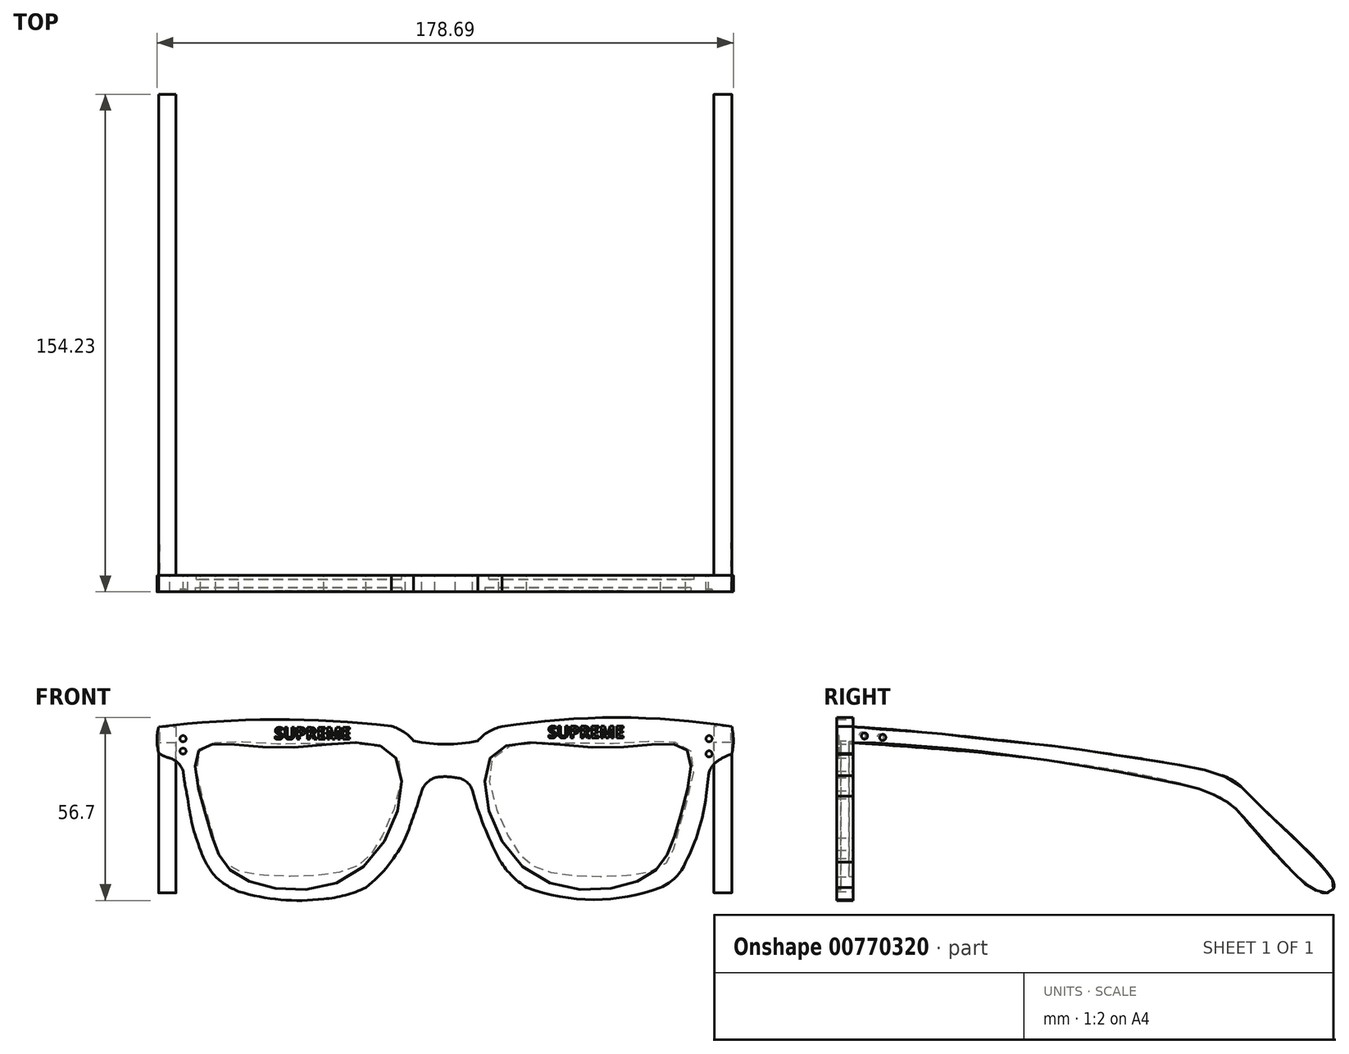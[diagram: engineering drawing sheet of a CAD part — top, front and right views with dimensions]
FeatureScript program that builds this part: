
annotation { "Feature Type Name" : "Feature", "Feature Type Description" : "" }
export const myFeature = defineFeature(function(context is Context, id is Id, definition is map)
    precondition{}
    {
        {
            var Q0;
            Q0=qCreatedBy(makeId("Front.planeOp"),FACE);
            var sketch = newSketch(context, id + "F0", { "sketchPlane" : qUnion([Q0])});
            skArc(sketch, "E0", {"start": v(-13.5, 37.38) * mm, "mid": v(-49.59, 39.43) * mm, "end": v(-85.66, 37.14) * mm});
            skArc(sketch, "E1", {"start": v(-6.56, 32.82) * mm, "mid": v(-9.67, 35.64) * mm, "end": v(-13.5, 37.38) * mm});
            skArc(sketch, "E2", {"start": v(-6.56, 32.82) * mm, "mid": v(3.35, 31.82) * mm, "end": v(13.26, 32.82) * mm});
            skArc(sketch, "E3", {"start": v(20.82, 37.23) * mm, "mid": v(16.66, 35.67) * mm, "end": v(13.26, 32.82) * mm});
            skArc(sketch, "E4", {"start": v(92.01, 37.23) * mm, "mid": v(56.41, 40.06) * mm, "end": v(20.82, 37.23) * mm});
            skArc(sketch, "E5", {"start": v(92.06, 28.92) * mm, "mid": v(92.54, 33.08) * mm, "end": v(92.01, 37.23) * mm});
            skArc(sketch, "E6", {"start": v(77.77, -4.76) * mm, "mid": v(81.8, 5.23) * mm, "end": v(84.08, 15.74) * mm});
            skArc(sketch, "E7", {"start": v(70.01, -12.62) * mm, "mid": v(74.63, -9.42) * mm, "end": v(77.77, -4.76) * mm});
            skArc(sketch, "E8", {"start": v(28.46, -12.62) * mm, "mid": v(49.23, -16.4) * mm, "end": v(70.01, -12.62) * mm});
            skArc(sketch, "E9", {"start": v(19.81, -3.65) * mm, "mid": v(23.57, -8.68) * mm, "end": v(28.46, -12.62) * mm});
            skArc(sketch, "E10", {"start": v(11.61, 17.3) * mm, "mid": v(15.15, 6.6) * mm, "end": v(19.81, -3.65) * mm});
            skArc(sketch, "E11", {"start": v(11.61, 17.3) * mm, "mid": v(9.68, 20.28) * mm, "end": v(6.3, 21.4) * mm});
            skArc(sketch, "E12", {"start": v(6.3, 21.4) * mm, "mid": v(3.15, 21.73) * mm, "end": v(0, 21.4) * mm});
            skArc(sketch, "E13", {"start": v(0, 21.4) * mm, "mid": v(-2.52, 19.8) * mm, "end": v(-4.12, 17.3) * mm});
            skArc(sketch, "E14", {"start": v(-9.1, 2.78) * mm, "mid": v(-6.43, 9.97) * mm, "end": v(-4.12, 17.3) * mm});
            skArc(sketch, "E15", {"start": v(-21.4, -12.62) * mm, "mid": v(-14.35, -5.65) * mm, "end": v(-9.1, 2.78) * mm});
            skArc(sketch, "E16", {"start": v(-34.48, -16.17) * mm, "mid": v(-27.78, -15.01) * mm, "end": v(-21.4, -12.62) * mm});
            skArc(sketch, "E17", {"start": v(-60.86, -13.84) * mm, "mid": v(-47.8, -16.4) * mm, "end": v(-34.48, -16.17) * mm});
            skArc(sketch, "E18", {"start": v(-67.95, -9.3) * mm, "mid": v(-64.61, -11.9) * mm, "end": v(-60.86, -13.84) * mm});
            skArc(sketch, "E19", {"start": v(-72.6, -1.1) * mm, "mid": v(-70.72, -5.45) * mm, "end": v(-67.95, -9.3) * mm});
            skArc(sketch, "E20", {"start": v(-76.6, 14.97) * mm, "mid": v(-75.16, 6.8) * mm, "end": v(-72.6, -1.1) * mm});
            skArc(sketch, "E21", {"start": v(-78.03, 23.4) * mm, "mid": v(-77.42, 19.16) * mm, "end": v(-76.6, 14.97) * mm});
            skArc(sketch, "E22", {"start": v(-78.03, 23.4) * mm, "mid": v(-79.58, 25.94) * mm, "end": v(-82.13, 27.5) * mm});
            skArc(sketch, "E23", {"start": v(-85.57, 29.04) * mm, "mid": v(-83.93, 28.09) * mm, "end": v(-82.13, 27.5) * mm});
            skArc(sketch, "E24", {"start": v(-85.66, 37.14) * mm, "mid": v(-86.15, 33.09) * mm, "end": v(-85.57, 29.04) * mm});
            skArc(sketch, "E25", {"start": v(91.85, 28.69) * mm, "mid": v(89.6, 27.74) * mm, "end": v(87.5, 26.49) * mm});
            skArc(sketch, "E26", {"start": v(91.81, 28.67) * mm, "mid": v(91.98, 28.77) * mm, "end": v(92.06, 28.94) * mm});
            skArc(sketch, "E27", {"start": v(87.5, 26.49) * mm, "mid": v(85.68, 24.53) * mm, "end": v(84.79, 22.01) * mm});
            skLineSegment(sketch, "E28", {"start": v(84.79, 22.01) * mm, "end": v(84.08, 15.74) * mm});
            skSolve(sketch);
        }
        {
            var Q0;
            Q0 = qSketchRegion(id + "F0", true);
            extrude(context, id + "F1", {"entities" : qUnion([Q0]), "depth" : 5.08 * mm, "offsetDistance" : 25.4 * mm});
        }
        {
            var Q0;
            Q0=makeQuery(id+"F1.opExtrude","CAP_FACE",FACE,{"disambiguationData":[OSD([sQuery(id+"F0.wireOp",EDGE,"E0"),sQuery(id+"F0.wireOp",EDGE,"E1"),sQuery(id+"F0.wireOp",EDGE,"E2"),sQuery(id+"F0.wireOp",EDGE,"E3"),sQuery(id+"F0.wireOp",EDGE,"E4"),sQuery(id+"F0.wireOp",EDGE,"E5"),sQuery(id+"F0.wireOp",EDGE,"E6"),sQuery(id+"F0.wireOp",EDGE,"E7"),sQuery(id+"F0.wireOp",EDGE,"E8"),sQuery(id+"F0.wireOp",EDGE,"E9"),sQuery(id+"F0.wireOp",EDGE,"E10"),sQuery(id+"F0.wireOp",EDGE,"E11"),sQuery(id+"F0.wireOp",EDGE,"E12"),sQuery(id+"F0.wireOp",EDGE,"E13"),sQuery(id+"F0.wireOp",EDGE,"E14"),sQuery(id+"F0.wireOp",EDGE,"E15"),sQuery(id+"F0.wireOp",EDGE,"E16"),sQuery(id+"F0.wireOp",EDGE,"E17"),sQuery(id+"F0.wireOp",EDGE,"E18"),sQuery(id+"F0.wireOp",EDGE,"E19"),sQuery(id+"F0.wireOp",EDGE,"E20"),sQuery(id+"F0.wireOp",EDGE,"E21"),sQuery(id+"F0.wireOp",EDGE,"E22"),sQuery(id+"F0.wireOp",EDGE,"E23"),sQuery(id+"F0.wireOp",EDGE,"E24"),sQuery(id+"F0.wireOp",EDGE,"E25"),sQuery(id+"F0.wireOp",EDGE,"E26"),sQuery(id+"F0.wireOp",EDGE,"E27"),sQuery(id+"F0.wireOp",EDGE,"E28")])],"isStart":false});
            var sketch = newSketch(context, id + "F2", { "sketchPlane" : qUnion([Q0])});
            skFitSpline(sketch, "E29", {"points": [v(-73.12, 29.88) * mm, v(-47.85, 30.68) * mm, v(-12.75, 28.55) * mm, v(-23.12, -7.08) * mm, v(-61.02, -8.94) * mm, v(-70.32, 7.4) * mm, v(-73.12, 29.88) * mm]});
            skFitSpline(sketch, "E30.MirrorC", {"points": [v(78.24, 29.88) * mm, v(52.98, 30.68) * mm, v(17.88, 28.55) * mm, v(28.25, -7.08) * mm, v(66.14, -8.94) * mm, v(75.45, 7.4) * mm, v(78.24, 29.88) * mm]});
            skSolve(sketch);
        }
        {
            var Q0;
            Q0 = qSketchRegion(id + "F2", true);
            extrude(context, id + "F3", {"entities" : qUnion([Q0]), "operationType" : NewBodyOperationType.REMOVE, "oppositeDirection" : true, "depth" : 1.27 * mm, "offsetDistance" : 25.4 * mm});
        }
        {
            var Q0;
            Q0=makeQuery(id+"F1.opExtrude","CAP_FACE",FACE,{"disambiguationData":[OSD([sQuery(id+"F0.wireOp",EDGE,"E0"),sQuery(id+"F0.wireOp",EDGE,"E1"),sQuery(id+"F0.wireOp",EDGE,"E2"),sQuery(id+"F0.wireOp",EDGE,"E3"),sQuery(id+"F0.wireOp",EDGE,"E4"),sQuery(id+"F0.wireOp",EDGE,"E5"),sQuery(id+"F0.wireOp",EDGE,"E6"),sQuery(id+"F0.wireOp",EDGE,"E7"),sQuery(id+"F0.wireOp",EDGE,"E8"),sQuery(id+"F0.wireOp",EDGE,"E9"),sQuery(id+"F0.wireOp",EDGE,"E10"),sQuery(id+"F0.wireOp",EDGE,"E11"),sQuery(id+"F0.wireOp",EDGE,"E12"),sQuery(id+"F0.wireOp",EDGE,"E13"),sQuery(id+"F0.wireOp",EDGE,"E14"),sQuery(id+"F0.wireOp",EDGE,"E15"),sQuery(id+"F0.wireOp",EDGE,"E16"),sQuery(id+"F0.wireOp",EDGE,"E17"),sQuery(id+"F0.wireOp",EDGE,"E18"),sQuery(id+"F0.wireOp",EDGE,"E19"),sQuery(id+"F0.wireOp",EDGE,"E20"),sQuery(id+"F0.wireOp",EDGE,"E21"),sQuery(id+"F0.wireOp",EDGE,"E22"),sQuery(id+"F0.wireOp",EDGE,"E23"),sQuery(id+"F0.wireOp",EDGE,"E24"),sQuery(id+"F0.wireOp",EDGE,"E25"),sQuery(id+"F0.wireOp",EDGE,"E26"),sQuery(id+"F0.wireOp",EDGE,"E27"),sQuery(id+"F0.wireOp",EDGE,"E28")])],"isStart":true});
            var sketch = newSketch(context, id + "F4", { "sketchPlane" : qUnion([Q0])});
            skFitSpline(sketch, "E31", {"points": [v(-79.44, 29.57) * mm, v(-53.26, 31.93) * mm, v(-18.19, 27.95) * mm, v(-22.34, 4.15) * mm, v(-31.45, -6.46) * mm, v(-51.31, -9.2) * mm, v(-70.95, -5.77) * mm, v(-75.57, 5.26) * mm, v(-79.44, 29.57) * mm]});
            skFitSpline(sketch, "E32.MirrorC", {"points": [v(73.03, 29.57) * mm, v(46.84, 31.93) * mm, v(11.77, 27.95) * mm, v(15.92, 4.15) * mm, v(25.03, -6.46) * mm, v(44.9, -9.2) * mm, v(64.53, -5.77) * mm, v(69.15, 5.26) * mm, v(73.03, 29.57) * mm]});
            skSolve(sketch);
        }
        {
            var Q0;
            Q0=makeQuery(id+"F4.imprint","IMPRINT",FACE,{"disambiguationData":[TD([[makeQuery(id+"F4.imprint","IMPRINT",EDGE,{"derivedFrom":sQuery(id+"F4.wireOp",EDGE,"E31")}),-1.0]])]});
            var Q1;
            Q1=makeQuery(id+"F4.imprint","IMPRINT",FACE,{"disambiguationData":[TD([[makeQuery(id+"F4.imprint","IMPRINT",EDGE,{"derivedFrom":sQuery(id+"F4.wireOp",EDGE,"E32.MirrorC")}),1.0]])]});
            extrude(context, id + "F5", {"entities" : qUnion([Q0, Q1]), "operationType" : NewBodyOperationType.REMOVE, "oppositeDirection" : true, "depth" : 1.27 * mm, "offsetDistance" : 25.4 * mm});
        }
        {
            var Q0;
            Q0=makeQuery(id+"F1.opExtrude","CAP_FACE",FACE,{"disambiguationData":[OSD([sQuery(id+"F0.wireOp",EDGE,"E0"),sQuery(id+"F0.wireOp",EDGE,"E1"),sQuery(id+"F0.wireOp",EDGE,"E2"),sQuery(id+"F0.wireOp",EDGE,"E3"),sQuery(id+"F0.wireOp",EDGE,"E4"),sQuery(id+"F0.wireOp",EDGE,"E5"),sQuery(id+"F0.wireOp",EDGE,"E6"),sQuery(id+"F0.wireOp",EDGE,"E7"),sQuery(id+"F0.wireOp",EDGE,"E8"),sQuery(id+"F0.wireOp",EDGE,"E9"),sQuery(id+"F0.wireOp",EDGE,"E10"),sQuery(id+"F0.wireOp",EDGE,"E11"),sQuery(id+"F0.wireOp",EDGE,"E12"),sQuery(id+"F0.wireOp",EDGE,"E13"),sQuery(id+"F0.wireOp",EDGE,"E14"),sQuery(id+"F0.wireOp",EDGE,"E15"),sQuery(id+"F0.wireOp",EDGE,"E16"),sQuery(id+"F0.wireOp",EDGE,"E17"),sQuery(id+"F0.wireOp",EDGE,"E18"),sQuery(id+"F0.wireOp",EDGE,"E19"),sQuery(id+"F0.wireOp",EDGE,"E20"),sQuery(id+"F0.wireOp",EDGE,"E21"),sQuery(id+"F0.wireOp",EDGE,"E22"),sQuery(id+"F0.wireOp",EDGE,"E23"),sQuery(id+"F0.wireOp",EDGE,"E24"),sQuery(id+"F0.wireOp",EDGE,"E25"),sQuery(id+"F0.wireOp",EDGE,"E26"),sQuery(id+"F0.wireOp",EDGE,"E27"),sQuery(id+"F0.wireOp",EDGE,"E28")])],"isStart":false});
            var sketch = newSketch(context, id + "F6", { "sketchPlane" : qUnion([Q0])});
            skCircle(sketch, "E33", {"center": v(-78.07, 33.5) * mm, "radius": 0.95 * mm});
            skCircle(sketch, "E34", {"center": v(-78.07, 29.66) * mm, "radius": 0.94 * mm});
            skCircle(sketch, "E35", {"center": v(85, 33.5) * mm, "radius": 0.95 * mm});
            skCircle(sketch, "E36", {"center": v(85, 28.8) * mm, "radius": 0.95 * mm});
            skSolve(sketch);
        }
        {
            var Q0;
            Q0=makeQuery(id+"F6.imprint","IMPRINT",FACE,{"disambiguationData":[TD([[makeQuery(id+"F6.imprint","IMPRINT",EDGE,{"derivedFrom":sQuery(id+"F6.wireOp",EDGE,"E34")}),1.0]])]});
            var Q1;
            Q1=makeQuery(id+"F6.imprint","IMPRINT",FACE,{"disambiguationData":[TD([[makeQuery(id+"F6.imprint","IMPRINT",EDGE,{"derivedFrom":sQuery(id+"F6.wireOp",EDGE,"E35")}),1.0]])]});
            var Q2;
            Q2=makeQuery(id+"F6.imprint","IMPRINT",FACE,{"disambiguationData":[TD([[makeQuery(id+"F6.imprint","IMPRINT",EDGE,{"derivedFrom":sQuery(id+"F6.wireOp",EDGE,"E36")}),1.0]])]});
            var Q3;
            Q3=makeQuery(id+"F6.imprint","IMPRINT",FACE,{"disambiguationData":[TD([[makeQuery(id+"F6.imprint","IMPRINT",EDGE,{"derivedFrom":sQuery(id+"F6.wireOp",EDGE,"E33")}),1.0]])]});
            extrude(context, id + "F7", {"entities" : qUnion([Q0, Q1, Q2, Q3]), "operationType" : NewBodyOperationType.REMOVE, "oppositeDirection" : true, "depth" : 0.76 * mm, "offsetDistance" : 25.4 * mm});
        }
        {
            var Q0;
            Q0=makeQuery(id+"F1.opExtrude","CAP_FACE",FACE,{"disambiguationData":[OSD([sQuery(id+"F0.wireOp",EDGE,"E0"),sQuery(id+"F0.wireOp",EDGE,"E1"),sQuery(id+"F0.wireOp",EDGE,"E2"),sQuery(id+"F0.wireOp",EDGE,"E3"),sQuery(id+"F0.wireOp",EDGE,"E4"),sQuery(id+"F0.wireOp",EDGE,"E5"),sQuery(id+"F0.wireOp",EDGE,"E6"),sQuery(id+"F0.wireOp",EDGE,"E7"),sQuery(id+"F0.wireOp",EDGE,"E8"),sQuery(id+"F0.wireOp",EDGE,"E9"),sQuery(id+"F0.wireOp",EDGE,"E10"),sQuery(id+"F0.wireOp",EDGE,"E11"),sQuery(id+"F0.wireOp",EDGE,"E12"),sQuery(id+"F0.wireOp",EDGE,"E13"),sQuery(id+"F0.wireOp",EDGE,"E14"),sQuery(id+"F0.wireOp",EDGE,"E15"),sQuery(id+"F0.wireOp",EDGE,"E16"),sQuery(id+"F0.wireOp",EDGE,"E17"),sQuery(id+"F0.wireOp",EDGE,"E18"),sQuery(id+"F0.wireOp",EDGE,"E19"),sQuery(id+"F0.wireOp",EDGE,"E20"),sQuery(id+"F0.wireOp",EDGE,"E21"),sQuery(id+"F0.wireOp",EDGE,"E22"),sQuery(id+"F0.wireOp",EDGE,"E23"),sQuery(id+"F0.wireOp",EDGE,"E24"),sQuery(id+"F0.wireOp",EDGE,"E25"),sQuery(id+"F0.wireOp",EDGE,"E26"),sQuery(id+"F0.wireOp",EDGE,"E27"),sQuery(id+"F0.wireOp",EDGE,"E28")])],"isStart":true});
            var sketch = newSketch(context, id + "F8", { "sketchPlane" : qUnion([Q0])});
            skLineSegment(sketch, "E37.bottom", {"start": v(85.66, 37.14) * mm, "end": v(80.25, 37.14) * mm});
            skLineSegment(sketch, "E37.top", {"start": v(85.66, -17.78) * mm, "end": v(80.25, -17.78) * mm});
            skLineSegment(sketch, "E37.left", {"start": v(85.66, 37.14) * mm, "end": v(85.66, -17.78) * mm});
            skLineSegment(sketch, "E37.right", {"start": v(80.25, 37.14) * mm, "end": v(80.25, -17.78) * mm});
            skSolve(sketch);
        }
        {
            var Q0;
            Q0 = qSketchRegion(id + "F8", true);
            extrude(context, id + "F9", {"entities" : qUnion([Q0]), "operationType" : NewBodyOperationType.ADD, "depth" : 152.4 * mm, "offsetDistance" : 25.4 * mm});
        }
        {
            var Q0;
            Q0=makeQuery(id+"F9.opExtrude","SWEPT_FACE",FACE,{"disambiguationData":[OSD([sQuery(id+"F8.wireOp",EDGE,"E37.left")])]});
            var sketch = newSketch(context, id + "F10", { "sketchPlane" : qUnion([Q0])});
            skFitSpline(sketch, "E38", {"points": [v(0, 37.14) * mm, v(-111.33, 23.08) * mm, v(-123.95, 14.92) * mm, v(-148.44, -9.87) * mm, v(-148.6, -13.41) * mm, v(-144.44, -13.88) * mm, v(-122.72, 7.06) * mm, v(-113.18, 15.69) * mm, v(-71.14, 25.38) * mm, v(-16.47, 31.08) * mm, v(9.4, 33.08) * mm, v(13.71, 34.62) * mm, v(10.94, 37.14) * mm, v(7.55, 37.14) * mm, v(0, 37.14) * mm]});
            skLineSegment(sketch, "E39", {"start": v(0, 37.14) * mm, "end": v(0, 32.22) * mm});
            skLineSegment(sketch, "E40", {"start": v(0, 32.22) * mm, "end": v(0, 37.14) * mm});
            skLineSegment(sketch, "E41", {"start": v(-148.6, -13.41) * mm, "end": v(-152.4, -17.78) * mm});
            skLineSegment(sketch, "E42", {"start": v(-152.4, -17.78) * mm, "end": v(-152.4, 37.14) * mm});
            skLineSegment(sketch, "E43", {"start": v(-152.4, 37.14) * mm, "end": v(0, 37.14) * mm});
            skLineSegment(sketch, "E44", {"start": v(-152.4, -17.78) * mm, "end": v(0, -17.78) * mm});
            skLineSegment(sketch, "E45", {"start": v(0, 32.22) * mm, "end": v(0, -17.78) * mm});
            skSolve(sketch);
        }
        {
            var Q0;
            {var subQ2=sQuery(id+"F10.wireOp",EDGE,"E41");Q0=makeQuery(id+"F10.imprint","IMPRINT",FACE,{"disambiguationData":[TD([[makeQuery(id+"F10.imprint","IMPRINT",EDGE,{"derivedFrom":subQ2}),-1.0]])]});}
            var Q1;
            {var subQ4=sQuery(id+"F10.wireOp",EDGE,"E41");Q1=makeQuery(id+"F10.imprint","IMPRINT",FACE,{"disambiguationData":[TD([[makeQuery(id+"F10.imprint","IMPRINT",EDGE,{"derivedFrom":subQ4}),1.0]])]});}
            extrude(context, id + "F11", {"entities" : qUnion([Q0, Q1]), "operationType" : NewBodyOperationType.REMOVE, "oppositeDirection" : true, "depth" : 25.4 * mm, "offsetDistance" : 25.4 * mm});
        }
        {
            var Q0;
            Q0=makeQuery(id+"F9.opExtrude","SWEPT_FACE",FACE,{"disambiguationData":[OSD([sQuery(id+"F8.wireOp",EDGE,"E37.left")])]});
            var sketch = newSketch(context, id + "F12", { "sketchPlane" : qUnion([Q0])});
            skCircle(sketch, "E46", {"center": v(-2.86, 34.46) * mm, "radius": 1.02 * mm});
            skCircle(sketch, "E47", {"center": v(-8.48, 33.91) * mm, "radius": 1.02 * mm});
            skSolve(sketch);
        }
        {
            var Q0;
            Q0=makeQuery(id+"F12.imprint","IMPRINT",FACE,{"disambiguationData":[TD([[makeQuery(id+"F12.imprint","IMPRINT",EDGE,{"derivedFrom":sQuery(id+"F12.wireOp",EDGE,"E47")}),1.0]])]});
            var Q1;
            Q1=makeQuery(id+"F12.imprint","IMPRINT",FACE,{"disambiguationData":[TD([[makeQuery(id+"F12.imprint","IMPRINT",EDGE,{"derivedFrom":sQuery(id+"F12.wireOp",EDGE,"E46")}),1.0]])]});
            extrude(context, id + "F13", {"entities" : qUnion([Q0, Q1]), "operationType" : NewBodyOperationType.REMOVE, "oppositeDirection" : true, "depth" : 0.25 * mm, "offsetDistance" : 25.4 * mm});
        }
        {
            var Q0;
            {var subQ0=sQuery(id+"F0.wireOp",EDGE,"E20");var subQ1=sQuery(id+"F0.wireOp",EDGE,"E19");var subQ2=sQuery(id+"F0.wireOp",EDGE,"E18");var subQ3=sQuery(id+"F0.wireOp",EDGE,"E17");var subQ4=sQuery(id+"F0.wireOp",EDGE,"E16");var subQ5=sQuery(id+"F0.wireOp",EDGE,"E15");var subQ6=sQuery(id+"F0.wireOp",EDGE,"E14");var subQ7=sQuery(id+"F0.wireOp",EDGE,"E13");var subQ8=sQuery(id+"F0.wireOp",EDGE,"E12");var subQ9=sQuery(id+"F0.wireOp",EDGE,"E11");var subQ10=sQuery(id+"F0.wireOp",EDGE,"E10");var subQ11=sQuery(id+"F0.wireOp",EDGE,"E9");var subQ12=sQuery(id+"F0.wireOp",EDGE,"E2");var subQ13=sQuery(id+"F8.wireOp",EDGE,"E37.right");var subQ14=sQuery(id+"F0.wireOp",EDGE,"E1");var subQ15=sQuery(id+"F8.wireOp",EDGE,"E37.left");var subQ16=makeQuery(id+"F9.opExtrude","SWEPT_FACE",FACE,{"disambiguationData":[OSD([subQ15])]});var subQ17=sQuery(id+"F0.wireOp",EDGE,"E28");var subQ18=sQuery(id+"F0.wireOp",EDGE,"E27");var subQ19=sQuery(id+"F0.wireOp",EDGE,"E26");var subQ20=sQuery(id+"F0.wireOp",EDGE,"E25");var subQ21=sQuery(id+"F0.wireOp",EDGE,"E24");var subQ22=sQuery(id+"F0.wireOp",EDGE,"E22");var subQ23=sQuery(id+"F0.wireOp",EDGE,"E21");var subQ24=sQuery(id+"F0.wireOp",EDGE,"E8");var subQ25=sQuery(id+"F0.wireOp",EDGE,"E7");var subQ26=sQuery(id+"F0.wireOp",EDGE,"E6");var subQ27=sQuery(id+"F0.wireOp",EDGE,"E5");var subQ28=sQuery(id+"F0.wireOp",EDGE,"E4");var subQ29=sQuery(id+"F0.wireOp",EDGE,"E3");var subQ30=sQuery(id+"F0.wireOp",EDGE,"E0");var subQ31=makeQuery(id+"F1.opExtrude","CAP_FACE",FACE,{"disambiguationData":[OSD([subQ30,subQ14,subQ12,subQ29,subQ28,subQ27,subQ26,subQ25,subQ24,subQ11,subQ10,subQ9,subQ8,subQ7,subQ6,subQ5,subQ4,subQ3,subQ2,subQ1,subQ0,subQ23,subQ22,sQuery(id+"F0.wireOp",EDGE,"E23"),subQ21,subQ20,subQ19,subQ18,subQ17])],"isStart":true});var subQ32=makeQuery(id+"F1.opExtrude","SWEPT_FACE",FACE,{"disambiguationData":[OSD([subQ30])]});var subQ33=sQuery(id+"F8.wireOp",EDGE,"E37.bottom");var subQ34=makeQuery(id+"F9.opExtrude","CAP_FACE",FACE,{"disambiguationData":[OSD([subQ33,sQuery(id+"F8.wireOp",EDGE,"E37.top"),subQ15,subQ13])],"isStart":true});var subQ35=makeQuery(id+"F1.opExtrude","SWEPT_FACE",FACE,{"disambiguationData":[OSD([subQ21])]});var subQ36=makeQuery(id+"F9.opExtrude","SWEPT_FACE",FACE,{"disambiguationData":[OSD([subQ33])]});var subQ37=subQ31;Q0=makeQuery(id+"F11.boolean.opBoolean","MERGE",FACE,{"derivedFrom":[makeQuery(id+"F9.boolean.opBoolean","SPLIT",FACE,{"disambiguationData":[TD([subQ32,subQ31,subQ35,subQ36,subQ34,subQ16])],"derivedFrom":subQ37}),makeQuery(id+"F9.boolean.opBoolean","SPLIT",FACE,{"disambiguationData":[TD([subQ32,subQ31,makeQuery(id+"F1.opExtrude","SWEPT_FACE",FACE,{"disambiguationData":[OSD([subQ14])]}),makeQuery(id+"F1.opExtrude","SWEPT_FACE",FACE,{"disambiguationData":[OSD([subQ12])]}),makeQuery(id+"F1.opExtrude","SWEPT_FACE",FACE,{"disambiguationData":[OSD([subQ29])]}),makeQuery(id+"F1.opExtrude","SWEPT_FACE",FACE,{"disambiguationData":[OSD([subQ28])]}),makeQuery(id+"F1.opExtrude","SWEPT_FACE",FACE,{"disambiguationData":[OSD([subQ27])]}),makeQuery(id+"F1.opExtrude","SWEPT_FACE",FACE,{"disambiguationData":[OSD([subQ26])]}),makeQuery(id+"F1.opExtrude","SWEPT_FACE",FACE,{"disambiguationData":[OSD([subQ25])]}),makeQuery(id+"F1.opExtrude","SWEPT_FACE",FACE,{"disambiguationData":[OSD([subQ24])]}),makeQuery(id+"F1.opExtrude","SWEPT_FACE",FACE,{"disambiguationData":[OSD([subQ11])]}),makeQuery(id+"F1.opExtrude","SWEPT_FACE",FACE,{"disambiguationData":[OSD([subQ10])]}),makeQuery(id+"F1.opExtrude","SWEPT_FACE",FACE,{"disambiguationData":[OSD([subQ9])]}),makeQuery(id+"F1.opExtrude","SWEPT_FACE",FACE,{"disambiguationData":[OSD([subQ8])]}),makeQuery(id+"F1.opExtrude","SWEPT_FACE",FACE,{"disambiguationData":[OSD([subQ7])]}),makeQuery(id+"F1.opExtrude","SWEPT_FACE",FACE,{"disambiguationData":[OSD([subQ6])]}),makeQuery(id+"F1.opExtrude","SWEPT_FACE",FACE,{"disambiguationData":[OSD([subQ5])]}),makeQuery(id+"F1.opExtrude","SWEPT_FACE",FACE,{"disambiguationData":[OSD([subQ4])]}),makeQuery(id+"F1.opExtrude","SWEPT_FACE",FACE,{"disambiguationData":[OSD([subQ3])]}),makeQuery(id+"F1.opExtrude","SWEPT_FACE",FACE,{"disambiguationData":[OSD([subQ2])]}),makeQuery(id+"F1.opExtrude","SWEPT_FACE",FACE,{"disambiguationData":[OSD([subQ1])]}),makeQuery(id+"F1.opExtrude","SWEPT_FACE",FACE,{"disambiguationData":[OSD([subQ0])]}),makeQuery(id+"F1.opExtrude","SWEPT_FACE",FACE,{"disambiguationData":[OSD([subQ23])]}),makeQuery(id+"F1.opExtrude","SWEPT_FACE",FACE,{"disambiguationData":[OSD([subQ22])]}),subQ35,makeQuery(id+"F1.opExtrude","SWEPT_FACE",FACE,{"disambiguationData":[OSD([subQ20])]}),makeQuery(id+"F1.opExtrude","SWEPT_FACE",FACE,{"disambiguationData":[OSD([subQ19])]}),makeQuery(id+"F1.opExtrude","SWEPT_FACE",FACE,{"disambiguationData":[OSD([subQ18])]}),makeQuery(id+"F1.opExtrude","SWEPT_FACE",FACE,{"disambiguationData":[OSD([subQ17])]}),makeQuery(id+"F5.boolean.opBoolean","COPY",FACE,{"derivedFrom":makeQuery(id+"F5.opExtrude","SWEPT_FACE",FACE,{"disambiguationData":[OSD([sQuery(id+"F4.wireOp",EDGE,"E31")])]})}),makeQuery(id+"F5.boolean.opBoolean","COPY",FACE,{"derivedFrom":makeQuery(id+"F5.opExtrude","SWEPT_FACE",FACE,{"disambiguationData":[OSD([sQuery(id+"F4.wireOp",EDGE,"E32.MirrorC")])]})}),subQ36,subQ34,subQ16,makeQuery(id+"F9.opExtrude","SWEPT_FACE",FACE,{"disambiguationData":[OSD([subQ13])]})])],"derivedFrom":subQ37}),makeQuery(id+"F11.opExtrude","SWEPT_FACE",FACE,{"disambiguationData":[OSD([sQuery(id+"F10.wireOp",EDGE,"E45")])]})]});}
            var sketch = newSketch(context, id + "F14", { "sketchPlane" : qUnion([Q0])});
            skLineSegment(sketch, "E48.bottom", {"start": v(-92.01, 37.23) * mm, "end": v(-86.51, 37.23) * mm});
            skLineSegment(sketch, "E48.top", {"start": v(-92.01, -16.74) * mm, "end": v(-86.51, -16.74) * mm});
            skLineSegment(sketch, "E48.left", {"start": v(-92.01, 37.23) * mm, "end": v(-92.01, -16.74) * mm});
            skLineSegment(sketch, "E48.right", {"start": v(-86.51, 37.23) * mm, "end": v(-86.51, -16.74) * mm});
            skSolve(sketch);
        }
        {
            var Q0;
            {var subQ1=sQuery(id+"F14.wireOp",EDGE,"E48.bottom");Q0=makeQuery(id+"F14.imprint","IMPRINT",FACE,{"disambiguationData":[TD([[makeQuery(id+"F14.imprint","IMPRINT",EDGE,{"derivedFrom":subQ1}),-1.0]])]});}
            var Q1;
            {var subQ2=sQuery(id+"F14.wireOp",EDGE,"E48.top");Q1=makeQuery(id+"F14.imprint","IMPRINT",FACE,{"disambiguationData":[TD([[makeQuery(id+"F14.imprint","IMPRINT",EDGE,{"derivedFrom":subQ2}),1.0]])]});}
            extrude(context, id + "F15", {"entities" : qUnion([Q0, Q1]), "operationType" : NewBodyOperationType.ADD, "depth" : 152.4 * mm, "offsetDistance" : 25.4 * mm});
        }
        {
            var Q0;
            Q0=makeQuery(id+"F15.opExtrude","SWEPT_FACE",FACE,{"disambiguationData":[OSD([sQuery(id+"F14.wireOp",EDGE,"E48.right")])]});
            var sketch = newSketch(context, id + "F16", { "sketchPlane" : qUnion([Q0])});
            skFitSpline(sketch, "E49", {"points": [v(0, 37.23) * mm, v(-23.26, 35.39) * mm, v(-41.27, 33.35) * mm, v(-62.63, 31.14) * mm, v(-80.76, 28.5) * mm, v(-96.33, 26.17) * mm, v(-112.46, 22.86) * mm, v(-120.52, 18.47) * mm, v(-125.99, 12.91) * mm, v(-134.6, 4.76) * mm, v(-144, -4.65) * mm, v(-147.13, -8.14) * mm, v(-149.02, -11.2) * mm, v(-148.84, -13.07) * mm, v(-147.13, -14.24) * mm, v(-142.65, -13.16) * mm, v(-135.67, -7.16) * mm, v(-120.8, 9.5) * mm, v(-117.57, 12.73) * mm, v(-111.2, 16.4) * mm, v(-99.83, 19.8) * mm, v(-54.96, 27.57) * mm, v(-22.67, 31.1) * mm, v(0, 32.3) * mm, v(7.45, 33.48) * mm, v(5.45, 37.23) * mm, v(0, 37.23) * mm]});
            skLineSegment(sketch, "E50", {"start": v(0, 37.23) * mm, "end": v(0, 32.3) * mm});
            skLineSegment(sketch, "E51", {"start": v(-148.84, -13.07) * mm, "end": v(-152.4, -16.74) * mm});
            skLineSegment(sketch, "E52", {"start": v(-152.4, -16.74) * mm, "end": v(-152.4, 37.23) * mm});
            skLineSegment(sketch, "E53", {"start": v(-152.4, 37.23) * mm, "end": v(0, 37.23) * mm});
            skLineSegment(sketch, "E54", {"start": v(-152.4, -16.74) * mm, "end": v(0, -16.74) * mm});
            skLineSegment(sketch, "E55", {"start": v(0, -16.74) * mm, "end": v(0, 32.3) * mm});
            skSolve(sketch);
        }
        {
            var Q0;
            {var subQ2=sQuery(id+"F16.wireOp",EDGE,"E51");Q0=makeQuery(id+"F16.imprint","IMPRINT",FACE,{"disambiguationData":[TD([[makeQuery(id+"F16.imprint","IMPRINT",EDGE,{"derivedFrom":subQ2}),-1.0]])]});}
            var Q1;
            {var subQ4=sQuery(id+"F16.wireOp",EDGE,"E51");Q1=makeQuery(id+"F16.imprint","IMPRINT",FACE,{"disambiguationData":[TD([[makeQuery(id+"F16.imprint","IMPRINT",EDGE,{"derivedFrom":subQ4}),1.0]])]});}
            extrude(context, id + "F17", {"entities" : qUnion([Q0, Q1]), "operationType" : NewBodyOperationType.REMOVE, "oppositeDirection" : true, "depth" : 25.4 * mm, "offsetDistance" : 25.4 * mm});
        }
        {
            var Q0;
            Q0=makeQuery(id+"F15.opExtrude","SWEPT_FACE",FACE,{"disambiguationData":[OSD([sQuery(id+"F14.wireOp",EDGE,"E48.left")])]});
            var sketch = newSketch(context, id + "F18", { "sketchPlane" : qUnion([Q0])});
            skCircle(sketch, "E56", {"center": v(3.58, 34.33) * mm, "radius": 0.95 * mm});
            skCircle(sketch, "E57", {"center": v(9.22, 33.9) * mm, "radius": 0.95 * mm});
            skSolve(sketch);
        }
        {
            var Q0;
            Q0 = qSketchRegion(id + "F18", true);
            extrude(context, id + "F19", {"entities" : qUnion([Q0]), "operationType" : NewBodyOperationType.REMOVE, "oppositeDirection" : true, "depth" : 0.25 * mm, "offsetDistance" : 25.4 * mm});
        }
        {
            var Q0;
            Q0=makeQuery(id+"F1.opExtrude","CAP_FACE",FACE,{"disambiguationData":[OSD([sQuery(id+"F0.wireOp",EDGE,"E0"),sQuery(id+"F0.wireOp",EDGE,"E1"),sQuery(id+"F0.wireOp",EDGE,"E2"),sQuery(id+"F0.wireOp",EDGE,"E3"),sQuery(id+"F0.wireOp",EDGE,"E4"),sQuery(id+"F0.wireOp",EDGE,"E5"),sQuery(id+"F0.wireOp",EDGE,"E6"),sQuery(id+"F0.wireOp",EDGE,"E7"),sQuery(id+"F0.wireOp",EDGE,"E8"),sQuery(id+"F0.wireOp",EDGE,"E9"),sQuery(id+"F0.wireOp",EDGE,"E10"),sQuery(id+"F0.wireOp",EDGE,"E11"),sQuery(id+"F0.wireOp",EDGE,"E12"),sQuery(id+"F0.wireOp",EDGE,"E13"),sQuery(id+"F0.wireOp",EDGE,"E14"),sQuery(id+"F0.wireOp",EDGE,"E15"),sQuery(id+"F0.wireOp",EDGE,"E16"),sQuery(id+"F0.wireOp",EDGE,"E17"),sQuery(id+"F0.wireOp",EDGE,"E18"),sQuery(id+"F0.wireOp",EDGE,"E19"),sQuery(id+"F0.wireOp",EDGE,"E20"),sQuery(id+"F0.wireOp",EDGE,"E21"),sQuery(id+"F0.wireOp",EDGE,"E22"),sQuery(id+"F0.wireOp",EDGE,"E23"),sQuery(id+"F0.wireOp",EDGE,"E24"),sQuery(id+"F0.wireOp",EDGE,"E25"),sQuery(id+"F0.wireOp",EDGE,"E26"),sQuery(id+"F0.wireOp",EDGE,"E27"),sQuery(id+"F0.wireOp",EDGE,"E28")])],"isStart":false});
            var sketch = newSketch(context, id + "F20", { "sketchPlane" : qUnion([Q0])});
            skText(sketch, "E58", { "text": "SUPREME", "fontName": "OpenSans-Bold.ttf"});
            const initialGuessF20  = {"E58": [0.03504, 0.03375, 1, 0, 0.00366]};
            skSetInitialGuess(sketch, initialGuessF20);
            skSolve(sketch);
        }
        {
            var Q0;
            Q0 = qSketchRegion(id + "F20", true);
            extrude(context, id + "F21", {"entities" : qUnion([Q0]), "operationType" : NewBodyOperationType.REMOVE, "oppositeDirection" : true, "depth" : 0.25 * mm, "offsetDistance" : 25.4 * mm});
        }
        {
            var Q0;
            {var subQ0=sQuery(id+"F0.wireOp",EDGE,"E10");var subQ1=sQuery(id+"F0.wireOp",EDGE,"E9");var subQ2=sQuery(id+"F0.wireOp",EDGE,"E7");var subQ3=sQuery(id+"F0.wireOp",EDGE,"E20");var subQ4=sQuery(id+"F0.wireOp",EDGE,"E19");var subQ5=sQuery(id+"F0.wireOp",EDGE,"E28");var subQ6=sQuery(id+"F0.wireOp",EDGE,"E18");var subQ7=sQuery(id+"F0.wireOp",EDGE,"E27");var subQ8=sQuery(id+"F0.wireOp",EDGE,"E17");var subQ9=sQuery(id+"F0.wireOp",EDGE,"E26");var subQ10=sQuery(id+"F0.wireOp",EDGE,"E16");var subQ11=sQuery(id+"F0.wireOp",EDGE,"E25");var subQ12=sQuery(id+"F0.wireOp",EDGE,"E15");var subQ13=sQuery(id+"F0.wireOp",EDGE,"E14");var subQ14=sQuery(id+"F0.wireOp",EDGE,"E13");var subQ15=sQuery(id+"F0.wireOp",EDGE,"E12");var subQ16=sQuery(id+"F0.wireOp",EDGE,"E11");var subQ17=sQuery(id+"F0.wireOp",EDGE,"E2");var subQ18=sQuery(id+"F0.wireOp",EDGE,"E1");var subQ19=sQuery(id+"F0.wireOp",EDGE,"E3");var subQ20=sQuery(id+"F0.wireOp",EDGE,"E21");var subQ21=sQuery(id+"F0.wireOp",EDGE,"E8");var subQ22=sQuery(id+"F0.wireOp",EDGE,"E0");var subQ23=sQuery(id+"F0.wireOp",EDGE,"E4");var subQ24=sQuery(id+"F0.wireOp",EDGE,"E5");var subQ25=sQuery(id+"F0.wireOp",EDGE,"E6");var subQ26=sQuery(id+"F0.wireOp",EDGE,"E22");var subQ27=sQuery(id+"F0.wireOp",EDGE,"E23");var subQ28=sQuery(id+"F0.wireOp",EDGE,"E24");Q0=makeQuery(id+"F21.boolean.opBoolean","SPLIT",FACE,{"disambiguationData":[TD([makeQuery(id+"F1.opExtrude","SWEPT_FACE",FACE,{"disambiguationData":[OSD([subQ22])]})])],"derivedFrom":makeQuery(id+"F1.opExtrude","CAP_FACE",FACE,{"disambiguationData":[OSD([subQ22,subQ18,subQ17,subQ19,subQ23,subQ24,subQ25,subQ2,subQ21,subQ1,subQ0,subQ16,subQ15,subQ14,subQ13,subQ12,subQ10,subQ8,subQ6,subQ4,subQ3,subQ20,subQ26,subQ27,subQ28,subQ11,subQ9,subQ7,subQ5])],"isStart":false})});}
            var sketch = newSketch(context, id + "F22", { "sketchPlane" : qUnion([Q0])});
            skText(sketch, "E59", { "text": "SUPREME", "fontName": "OpenSans-Bold.ttf"});
            const initialGuessF22  = {"E59": [-0.04973, 0.03335, 1, 0, 0.00365]};
            skSetInitialGuess(sketch, initialGuessF22);
            skSolve(sketch);
        }
        {
            var Q0;
            Q0 = qSketchRegion(id + "F22", true);
            extrude(context, id + "F23", {"entities" : qUnion([Q0]), "operationType" : NewBodyOperationType.REMOVE, "oppositeDirection" : true, "depth" : 0.25 * mm, "offsetDistance" : 25.4 * mm});
        }
    });
